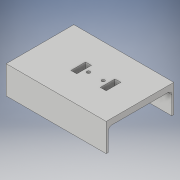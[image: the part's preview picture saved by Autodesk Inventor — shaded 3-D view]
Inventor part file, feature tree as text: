
AUTODESK INVENTOR PART (.ipt)
format: ipt  version: 2019 (Build 230136000, 136)  size: 294,912 bytes
history: native  units: in
note: dims shown in document units (in); Inventor stores cm internally (conversion verified against a paired STEP export)
features: sketch x12, extrude x10, projected_geometry x5, plane x2, fillet x2, emboss x1
ambient origin geometry x8: Origin, YZ Plane, XZ Plane, XY Plane, X Axis, Y Axis, Z Axis, Center Point
bodies: Solid1 (feature_tree)
feature tree (32):
  extrude  "Extrusion1"  Depth=3.4in
  extrude  "Extrusion6"  Depth=0.2in TaperAngle=0.0deg
  plane  "Work Plane1"
  extrude  "Extrusion7"  Depth=3.25in TaperAngle=0.0deg
  extrude  "Extrusion9"  Depth=0.15in TaperAngle=0.0deg
  extrude  "Extrusion12"  Depth=0.2in TaperAngle=0.0deg
  fillet  "Fillet7"  Radius=0.66in
  extrude  "Extrusion13"  Depth=0.2in TaperAngle=0.0deg
  extrude  "Extrusion14"  Depth=0.05in TaperAngle=0.0deg
  emboss  "Emboss2"
  plane  "Work Plane2"
  extrude  "Extrusion15"  Depth=0.5in
  sketch  "Sketch21"  dims[d92=0.7874in d94=1.0in d95=0.3937in d97=1.0in d99=0.05in d100=0.0in]
  extrude  "Extrusion16"  Depth=1.0in
  fillet  "Fillet10"  Radius=0.05in
  extrude  "Extrusion17"  Depth=0.25in
  sketch  "Sketch1"  dims[d0=2.3in d1=3.4in]
  sketch  "Sketch9"  dims[d2=0.5in d3=0.0in d23=0.2in d24=0.0in]
  projected_geometry  "Projected Loop4"
  sketch  "Sketch10"  dims[d26=0.4in d31=3.25in d32=0.0in]
  sketch  "Sketch12"  dims[d42=0.4in d43=0.0in d57=0.15in d58=0.0in]
  sketch  "Sketch16"  dims[d59=0.125in d60=0.2in d61=0.0in d62=0.66in d63=0.0in]
  sketch  "Sketch17"  dims[d65=0.05in d66=0.0in d74=0.2in d75=0.0in]
  projected_geometry  "Projected Loop7"
  sketch  "Sketch18"  dims[d77=0.3in d79=0.05in d80=0.0in]
  projected_geometry  "Projected Loop8"
  sketch  "Sketch19"  dims[d81=0.125in d89=0.5in]
  sketch  "Sketch20"  dims[d90=0.2in d91=1.0in]
  projected_geometry  "Projected Loop9"
  sketch  "Sketch22"  dims[d101=0.1094in d102=0.25in]
  projected_geometry  "Projected Loop10"
  sketch  "Sketch23"  dims[d103=0.25in d104=0.45in d105=0.07in d106=0.07in d107=0.15in]
